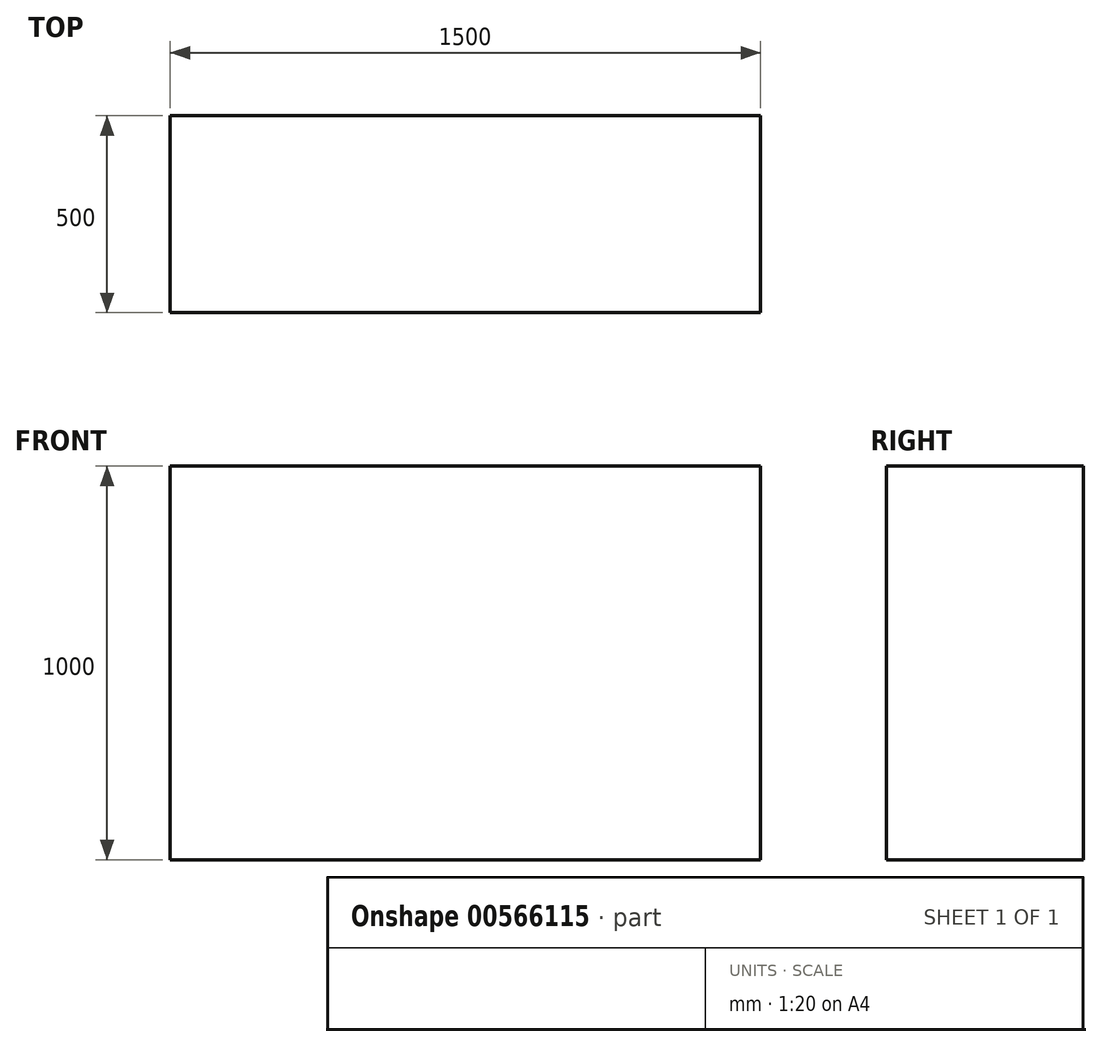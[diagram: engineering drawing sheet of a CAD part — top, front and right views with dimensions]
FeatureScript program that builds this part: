
annotation { "Feature Type Name" : "Feature", "Feature Type Description" : "" }
export const myFeature = defineFeature(function(context is Context, id is Id, definition is map)
    precondition{}
    {
        {
            var Q0;
            Q0=qCreatedBy(makeId("Front.planeOp"),FACE);
            var sketch = newSketch(context, id + "F0", { "sketchPlane" : qUnion([Q0])});
            skLineSegment(sketch, "E0.bottom", {"start": v(750, -500) * mm, "end": v(-750, -500) * mm});
            skLineSegment(sketch, "E0.top", {"start": v(750, 500) * mm, "end": v(-750, 500) * mm});
            skLineSegment(sketch, "E0.left", {"start": v(750, -500) * mm, "end": v(750, 500) * mm});
            skLineSegment(sketch, "E0.right", {"start": v(-750, -500) * mm, "end": v(-750, 500) * mm});
            skPoint(sketch, "E0.middle", {"position": v(0, 0) * mm});
            skSolve(sketch);
        }
        {
            var Q0;
            Q0 = qSketchRegion(id + "F0", true);
            extrude(context, id + "F1", {"entities" : qUnion([Q0]), "depth" : 500 * mm, "offsetDistance" : 25 * mm});
        }
        {
            var Q0;
            Q0=makeQuery(id+"F1.opExtrude","CAP_FACE",FACE,{"disambiguationData":[OSD([sQuery(id+"F0.wireOp",EDGE,"E0.bottom"),sQuery(id+"F0.wireOp",EDGE,"E0.top"),sQuery(id+"F0.wireOp",EDGE,"E0.left"),sQuery(id+"F0.wireOp",EDGE,"E0.right")])],"isStart":false});
            var sketch = newSketch(context, id + "F2", { "sketchPlane" : qUnion([Q0])});
            skSolve(sketch);
        }
        {
            var Q0;
            Q0=makeQuery(id+"F2.imprint","IMPRINT",FACE,{"disambiguationData":[TD([[makeQuery(id+"F2.imprint","IMPRINT",EDGE,{"derivedFrom":makeQuery(id+"F1.opExtrude","CAP_EDGE",EDGE,{"disambiguationData":[OSD([sQuery(id+"F0.wireOp",EDGE,"E0.bottom")])],"isStart":false})}),-1.0]])]});
            var sketch = newSketch(context, id + "F3", { "sketchPlane" : qUnion([Q0])});
            skLineSegment(sketch, "E1.bottom", {"start": v(-834.33, 0) * mm, "end": v(-2334.33, 0) * mm});
            skLineSegment(sketch, "E1.top", {"start": v(-834.33, 1000) * mm, "end": v(-2334.33, 1000) * mm});
            skLineSegment(sketch, "E1.left", {"start": v(-834.33, 0) * mm, "end": v(-834.33, 1000) * mm});
            skLineSegment(sketch, "E1.right", {"start": v(-2334.33, 0) * mm, "end": v(-2334.33, 1000) * mm});
            skPoint(sketch, "E1.middle", {"position": v(-1584.33, 500) * mm});
            skSolve(sketch);
        }
        {
            var Q0;
            Q0 = qSketchRegion(id + "F3", true);
            extrude(context, id + "F4", {"entities" : qUnion([Q0]), "depth" : 50 * mm, "offsetDistance" : 25 * mm});
        }
        {
            var Q0;
            Q0=makeQuery(id+"F4.opExtrude","SWEPT_BODY",BODY,{"disambiguationData":[OSD([sQuery(id+"F3.wireOp",EDGE,"E1.bottom"),sQuery(id+"F3.wireOp",EDGE,"E1.top"),sQuery(id+"F3.wireOp",EDGE,"E1.left"),sQuery(id+"F3.wireOp",EDGE,"E1.right")])]});
            deleteBodies(context, id + "F5", {"entities" : qUnion([Q0])});
        }
    });
